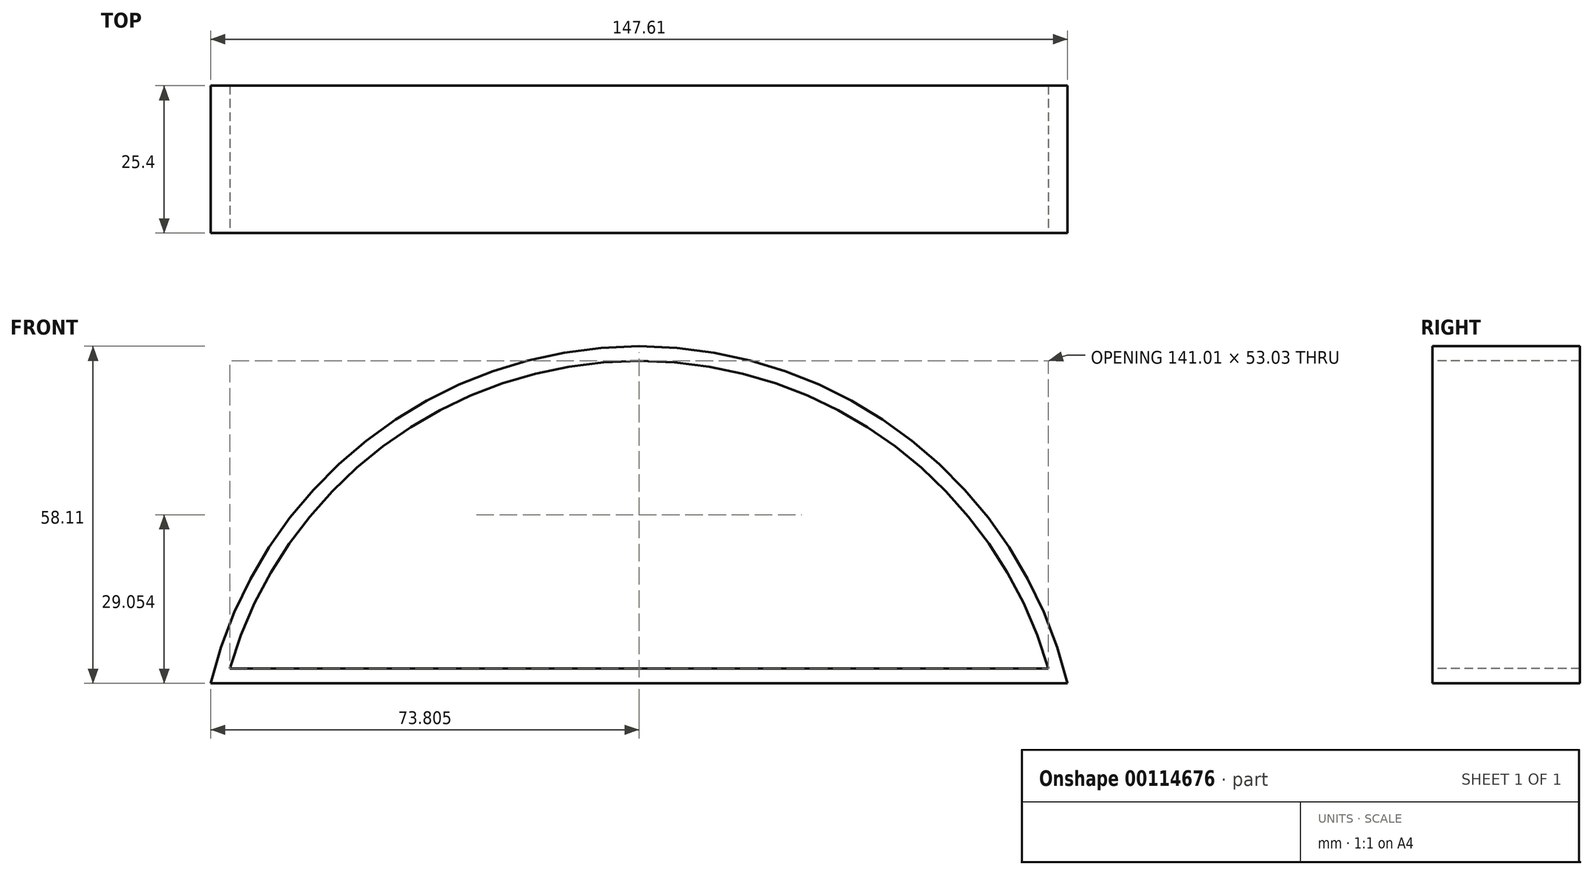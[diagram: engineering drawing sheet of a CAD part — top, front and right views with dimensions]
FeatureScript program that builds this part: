
annotation { "Feature Type Name" : "Feature", "Feature Type Description" : "" }
export const myFeature = defineFeature(function(context is Context, id is Id, definition is map)
    precondition{}
    {
        {
            var Q0;
            Q0=qCreatedBy(makeId("Front.planeOp"),FACE);
            var sketch = newSketch(context, id + "F1", { "sketchPlane" : qUnion([Q0])});
            skArc(sketch, "E0", {"start": v(79.48, 0) * mm, "mid": v(5.67, 58.1) * mm, "end": v(-68.13, 0) * mm});
            skLineSegment(sketch, "E1", {"start": v(-68.13, 0) * mm, "end": v(79.48, 0) * mm});
            skSolve(sketch);
        }
        {
            var Q0;
            Q0 = qSketchRegion(id + "F1", true);
            extrude(context, id + "F0", {"entities" : qUnion([Q0]), "oppositeDirection" : true, "depth" : 25.4 * mm});
        }
        {
            var Q0;
            Q0=makeQuery(id+"F0.opExtrude","CAP_FACE",FACE,{"disambiguationData":[OSD([sQuery(id+"F1.wireOp",EDGE,"E0"),sQuery(id+"F1.wireOp",EDGE,"E1")])],"isStart":false});
            var Q1;
            Q1=makeQuery(id+"F0.opExtrude","CAP_FACE",FACE,{"disambiguationData":[OSD([sQuery(id+"F1.wireOp",EDGE,"E0"),sQuery(id+"F1.wireOp",EDGE,"E1")])],"isStart":true});
            shell(context, id + "F2", {"entities" : qUnion([Q0, Q1]), "thickness" : 2.54 * mm});
        }
    });
